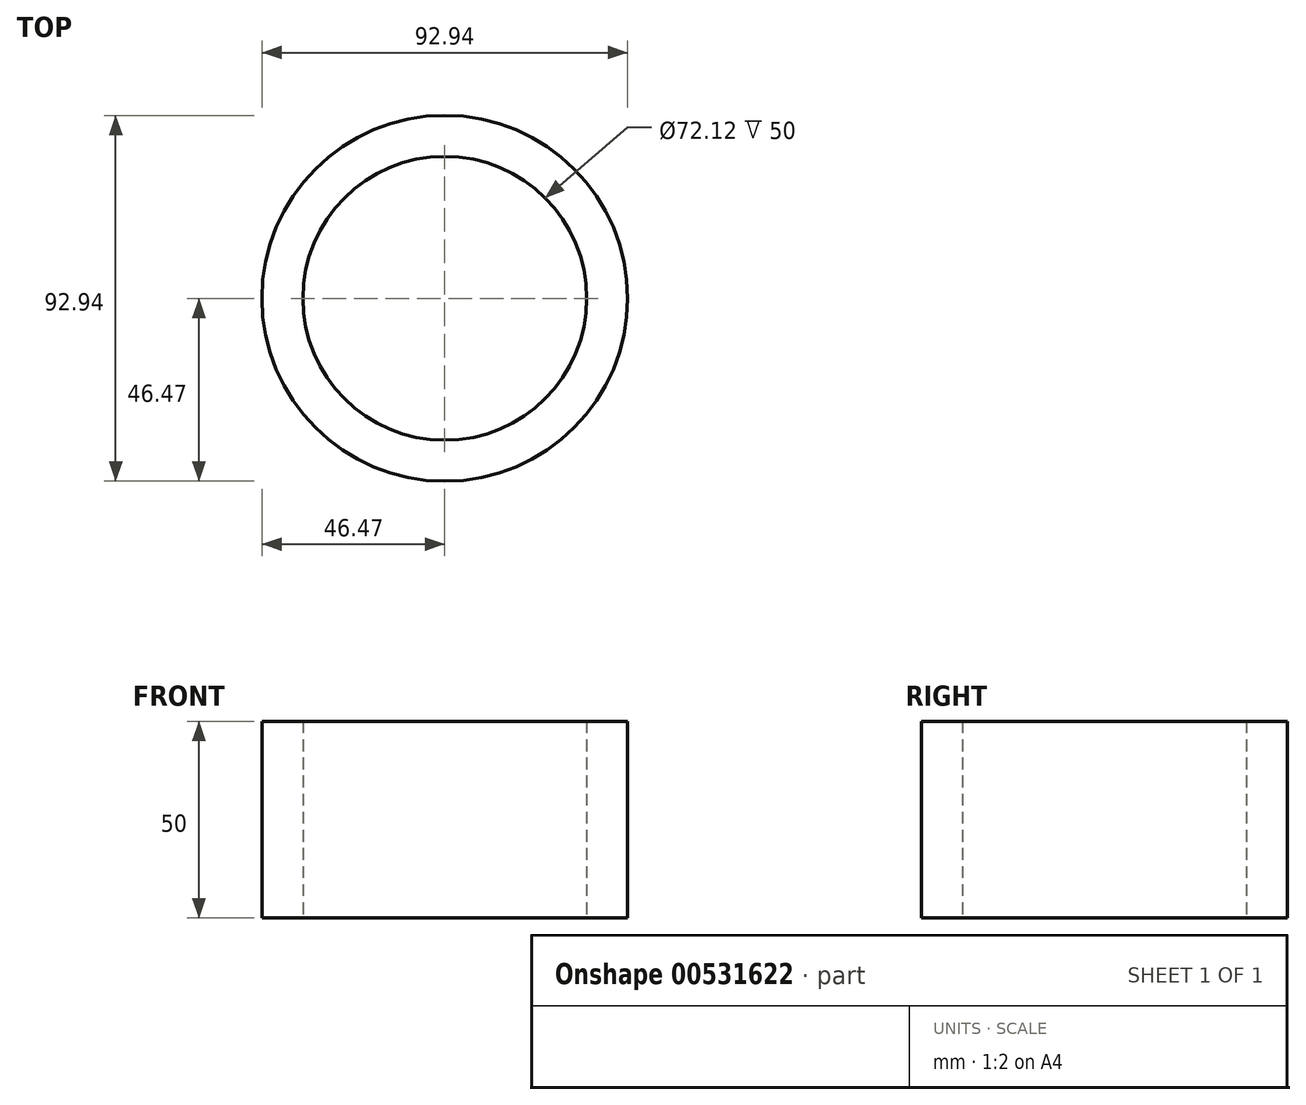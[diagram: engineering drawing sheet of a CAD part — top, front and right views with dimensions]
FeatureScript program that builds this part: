
annotation { "Feature Type Name" : "Feature", "Feature Type Description" : "" }
export const myFeature = defineFeature(function(context is Context, id is Id, definition is map)
    precondition{}
    {
        {
            var Q0;
            Q0=qCreatedBy(makeId("Top.planeOp"),FACE);
            var sketch = newSketch(context, id + "F0", { "sketchPlane" : qUnion([Q0])});
            skCircle(sketch, "E0", {"center": v(0, 0) * mm, "radius": 46.47 * mm});
            skCircle(sketch, "E1", {"center": v(0, 0) * mm, "radius": 36.06 * mm});
            skSolve(sketch);
        }
        {
            var Q0;
            Q0=makeQuery(id+"F0.imprint","IMPRINT",FACE,{"disambiguationData":[TD([[makeQuery(id+"F0.imprint","IMPRINT",EDGE,{"derivedFrom":sQuery(id+"F0.wireOp",EDGE,"E0")}),1.0]])]});
            extrude(context, id + "F1", {"entities" : qUnion([Q0]), "depth" : 50 * mm, "offsetDistance" : 25 * mm});
        }
    });
